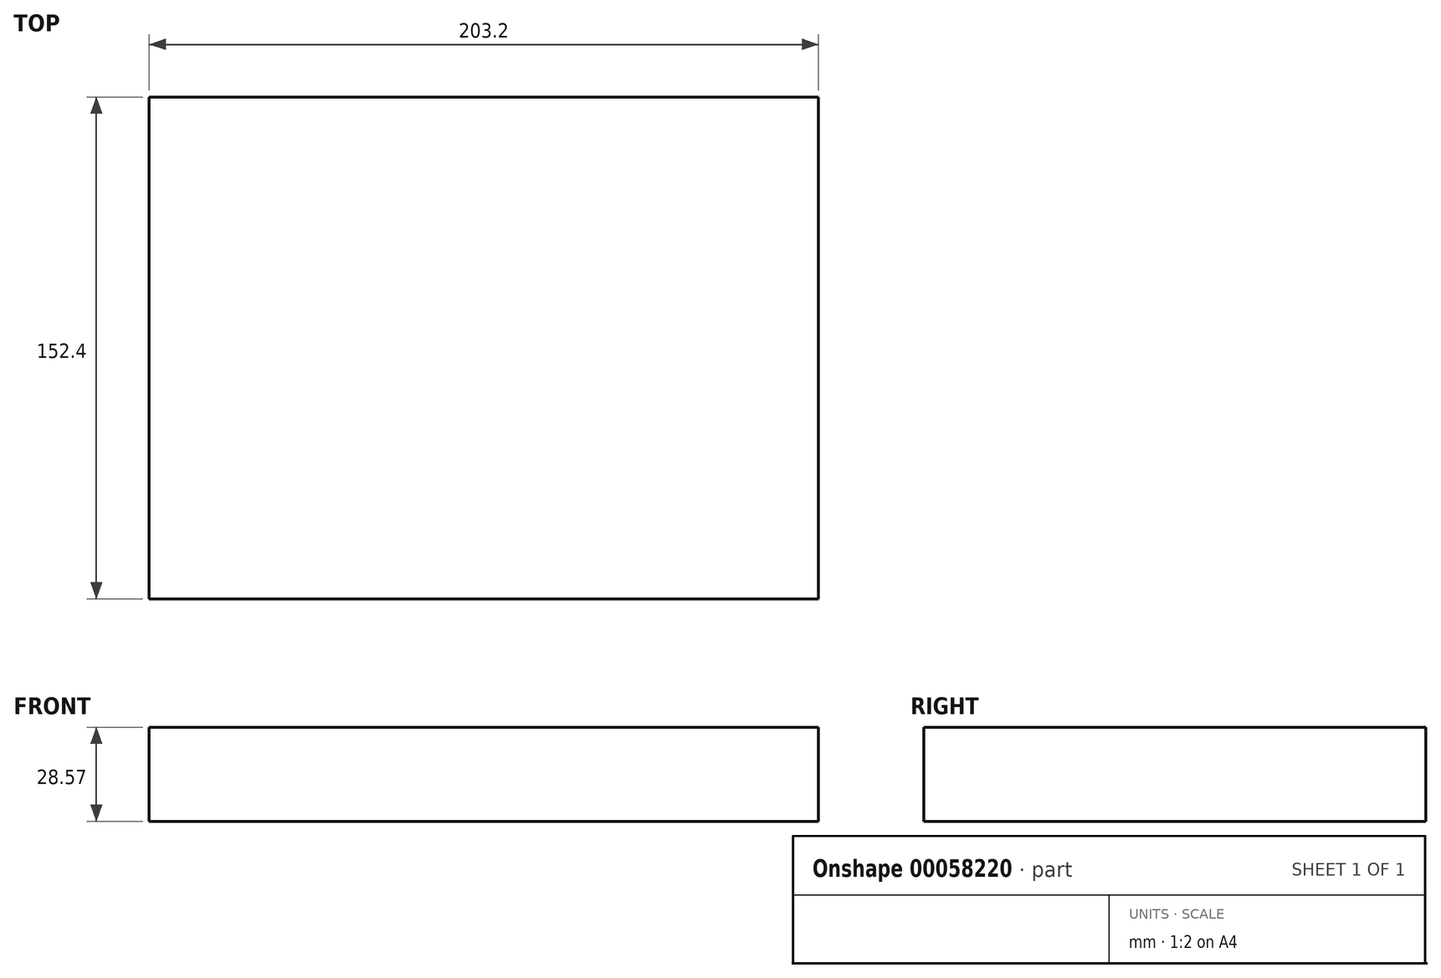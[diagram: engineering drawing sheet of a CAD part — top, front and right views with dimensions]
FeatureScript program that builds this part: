
annotation { "Feature Type Name" : "Feature", "Feature Type Description" : "" }
export const myFeature = defineFeature(function(context is Context, id is Id, definition is map)
    precondition{}
    {
        {
            var Q0;
            Q0=qCreatedBy(makeId("Top.planeOp"),FACE);
            var sketch = newSketch(context, id + "F0", { "sketchPlane" : qUnion([Q0])});
            skLineSegment(sketch, "E0.rect.bottom", {"start": v(101.6, -76.2) * mm, "end": v(-101.6, -76.2) * mm});
            skLineSegment(sketch, "E0.rect.top", {"start": v(101.6, 76.2) * mm, "end": v(-101.6, 76.2) * mm});
            skLineSegment(sketch, "E0.rect.left", {"start": v(101.6, -76.2) * mm, "end": v(101.6, 76.2) * mm});
            skLineSegment(sketch, "E0.rect.right", {"start": v(-101.6, -76.2) * mm, "end": v(-101.6, 76.2) * mm});
            skPoint(sketch, "E0.rect.middle", {"position": v(0, 0) * mm});
            skSolve(sketch);
        }
        {
            var Q0;
            Q0 = qSketchRegion(id + "F0", true);
            extrude(context, id + "F1", {"entities" : qUnion([Q0]), "depth" : 28.57 * mm});
        }
    });
